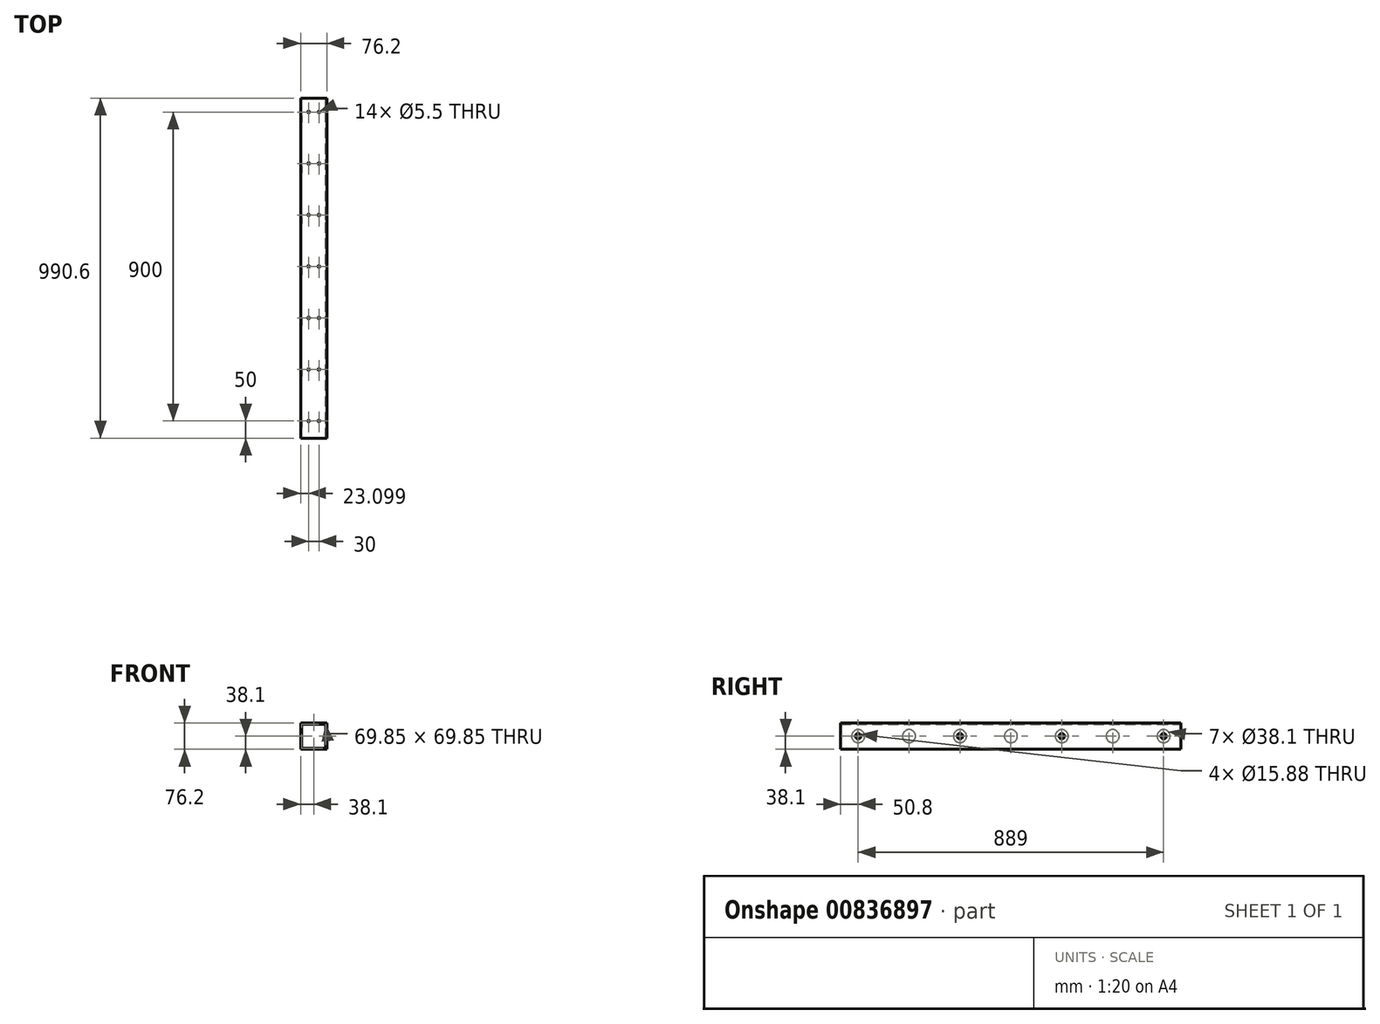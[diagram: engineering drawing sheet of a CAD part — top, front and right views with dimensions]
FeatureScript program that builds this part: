
annotation { "Feature Type Name" : "Feature", "Feature Type Description" : "" }
export const myFeature = defineFeature(function(context is Context, id is Id, definition is map)
    precondition{}
    {
        {
            var Q0;
            Q0=qCreatedBy(makeId("Front.planeOp"),FACE);
            var sketch = newSketch(context, id + "F0", { "sketchPlane" : qUnion([Q0])});
            skLineSegment(sketch, "E0.bottom", {"start": v(38.1, 38.1) * mm, "end": v(-38.1, 38.1) * mm});
            skLineSegment(sketch, "E0.top", {"start": v(38.1, -38.1) * mm, "end": v(-38.1, -38.1) * mm});
            skLineSegment(sketch, "E0.left", {"start": v(38.1, 38.1) * mm, "end": v(38.1, -38.1) * mm});
            skLineSegment(sketch, "E0.right", {"start": v(-38.1, 38.1) * mm, "end": v(-38.1, -38.1) * mm});
            skPoint(sketch, "E0.middle", {"position": v(0, 0) * mm});
            skLineSegment(sketch, "E1.bottom", {"start": v(34.93, 34.93) * mm, "end": v(-34.92, 34.93) * mm});
            skLineSegment(sketch, "E1.top", {"start": v(34.92, -34.92) * mm, "end": v(-34.93, -34.92) * mm});
            skLineSegment(sketch, "E1.left", {"start": v(34.93, 34.93) * mm, "end": v(34.92, -34.92) * mm});
            skLineSegment(sketch, "E1.right", {"start": v(-34.92, 34.93) * mm, "end": v(-34.93, -34.92) * mm});
            skSolve(sketch);
        }
        {
            var Q0;
            Q0 = qSketchRegion(id + "F0", true);
            extrude(context, id + "F1", {"entities" : qUnion([Q0]), "depth" : 990.6 * mm, "offsetDistance" : 25.4 * mm});
        }
        {
            var Q0;
            Q0=makeQuery(id+"F1.opExtrude","SWEPT_FACE",FACE,{"disambiguationData":[OSD([sQuery(id+"F0.wireOp",EDGE,"E0.bottom")])]});
            var sketch = newSketch(context, id + "F2", { "sketchPlane" : qUnion([Q0])});
            skCircle(sketch, "E2", {"center": v(-15, -940.6) * mm, "radius": 2.75 * mm});
            skCircle(sketch, "E3", {"center": v(15, -940.6) * mm, "radius": 2.75 * mm});
            skLineSegment(sketch, "E4", {"start": v(-15, -940.6) * mm, "end": v(15, -940.6) * mm, "construction": true});
            skLineSegment(sketch, "E5", {"start": v(0, -940.6) * mm, "end": v(0, -990.6) * mm, "construction": true});
            skLineSegment(sketch, "E6", {"start": v(0, -940.6) * mm, "end": v(0, -790.6) * mm, "construction": true});
            skCircle(sketch, "E7.0.1.0", {"center": v(15, -790.6) * mm, "radius": 2.75 * mm});
            skCircle(sketch, "E7.0.1.1", {"center": v(-15, -790.6) * mm, "radius": 2.75 * mm});
            skCircle(sketch, "E7.0.2.0", {"center": v(15, -640.6) * mm, "radius": 2.75 * mm});
            skCircle(sketch, "E7.0.2.1", {"center": v(-15, -640.6) * mm, "radius": 2.75 * mm});
            skCircle(sketch, "E7.0.3.0", {"center": v(15, -490.6) * mm, "radius": 2.75 * mm});
            skCircle(sketch, "E7.0.3.1", {"center": v(-15, -490.6) * mm, "radius": 2.75 * mm});
            skCircle(sketch, "E7.0.4.0", {"center": v(15, -340.6) * mm, "radius": 2.75 * mm});
            skCircle(sketch, "E7.0.4.1", {"center": v(-15, -340.6) * mm, "radius": 2.75 * mm});
            skCircle(sketch, "E7.0.5.0", {"center": v(15, -190.6) * mm, "radius": 2.75 * mm});
            skCircle(sketch, "E7.0.5.1", {"center": v(-15, -190.6) * mm, "radius": 2.75 * mm});
            skCircle(sketch, "E7.0.6.0", {"center": v(15, -40.6) * mm, "radius": 2.75 * mm});
            skCircle(sketch, "E7.0.6.1", {"center": v(-15, -40.6) * mm, "radius": 2.75 * mm});
            skLineSegment(sketch, "E7.direction1", {"start": v(-15, -940.6) * mm, "end": v(10.4, -940.6) * mm, "construction": true});
            skLineSegment(sketch, "E7.direction2", {"start": v(-15, -940.6) * mm, "end": v(-15, -790.6) * mm, "construction": true});
            skSolve(sketch);
        }
        {
            var Q0;
            Q0 = qSketchRegion(id + "F2", true);
            extrude(context, id + "F3", {"entities" : qUnion([Q0]), "operationType" : NewBodyOperationType.REMOVE, "oppositeDirection" : true, "depth" : 25.4 * mm, "offsetDistance" : 25.4 * mm});
        }
        {
            var Q0;
            Q0=makeQuery(id+"F1.opExtrude","SWEPT_FACE",FACE,{"disambiguationData":[OSD([sQuery(id+"F0.wireOp",EDGE,"E0.left")])]});
            var sketch = newSketch(context, id + "F4", { "sketchPlane" : qUnion([Q0])});
            skCircle(sketch, "E8", {"center": v(-939.8, 0) * mm, "radius": 7.94 * mm});
            skCircle(sketch, "E9", {"center": v(-643.47, 0) * mm, "radius": 7.94 * mm});
            skCircle(sketch, "E10", {"center": v(-347.13, 0) * mm, "radius": 7.94 * mm});
            skCircle(sketch, "E11", {"center": v(-50.8, 0) * mm, "radius": 7.94 * mm});
            skLineSegment(sketch, "E12", {"start": v(-939.8, 0) * mm, "end": v(-643.47, 0) * mm, "construction": true});
            skLineSegment(sketch, "E13", {"start": v(-643.47, 0) * mm, "end": v(-347.13, 0) * mm, "construction": true});
            skLineSegment(sketch, "E14", {"start": v(-347.13, 0) * mm, "end": v(-50.8, 0) * mm, "construction": true});
            skLineSegment(sketch, "E15", {"start": v(-939.8, 0) * mm, "end": v(-990.6, 0) * mm, "construction": true});
            skLineSegment(sketch, "E16", {"start": v(-50.8, 0) * mm, "end": v(0, 0) * mm, "construction": true});
            skSolve(sketch);
        }
        {
            var Q0;
            Q0 = qSketchRegion(id + "F4", true);
            extrude(context, id + "F5", {"entities" : qUnion([Q0]), "operationType" : NewBodyOperationType.REMOVE, "oppositeDirection" : true, "depth" : 25.4 * mm, "offsetDistance" : 25.4 * mm});
        }
        {
            var Q0;
            Q0=makeQuery(id+"F1.opExtrude","SWEPT_FACE",FACE,{"disambiguationData":[OSD([sQuery(id+"F0.wireOp",EDGE,"E0.right")])]});
            var sketch = newSketch(context, id + "F6", { "sketchPlane" : qUnion([Q0])});
            skCircle(sketch, "E17", {"center": v(643.47, 0) * mm, "radius": 19.05 * mm});
            skCircle(sketch, "E18", {"center": v(347.13, 0) * mm, "radius": 19.05 * mm});
            skCircle(sketch, "E19", {"center": v(50.8, 0) * mm, "radius": 19.05 * mm});
            skLineSegment(sketch, "E20", {"start": v(50.8, 0) * mm, "end": v(347.13, 0) * mm});
            skLineSegment(sketch, "E21", {"start": v(347.13, 0) * mm, "end": v(643.47, 0) * mm});
            skLineSegment(sketch, "E22", {"start": v(643.47, 0) * mm, "end": v(939.8, 0) * mm});
            skCircle(sketch, "E23", {"center": v(198.97, 0) * mm, "radius": 19.05 * mm});
            skCircle(sketch, "E24", {"center": v(495.3, 0) * mm, "radius": 19.05 * mm});
            skCircle(sketch, "E25", {"center": v(791.63, 0) * mm, "radius": 19.05 * mm});
            skCircle(sketch, "E26", {"center": v(939.8, 0) * mm, "radius": 19.05 * mm});
            skSolve(sketch);
        }
        {
            var Q0;
            Q0 = qSketchRegion(id + "F6", true);
            extrude(context, id + "F7", {"entities" : qUnion([Q0]), "operationType" : NewBodyOperationType.REMOVE, "oppositeDirection" : true, "depth" : 25.4 * mm, "offsetDistance" : 25.4 * mm});
        }
    });
